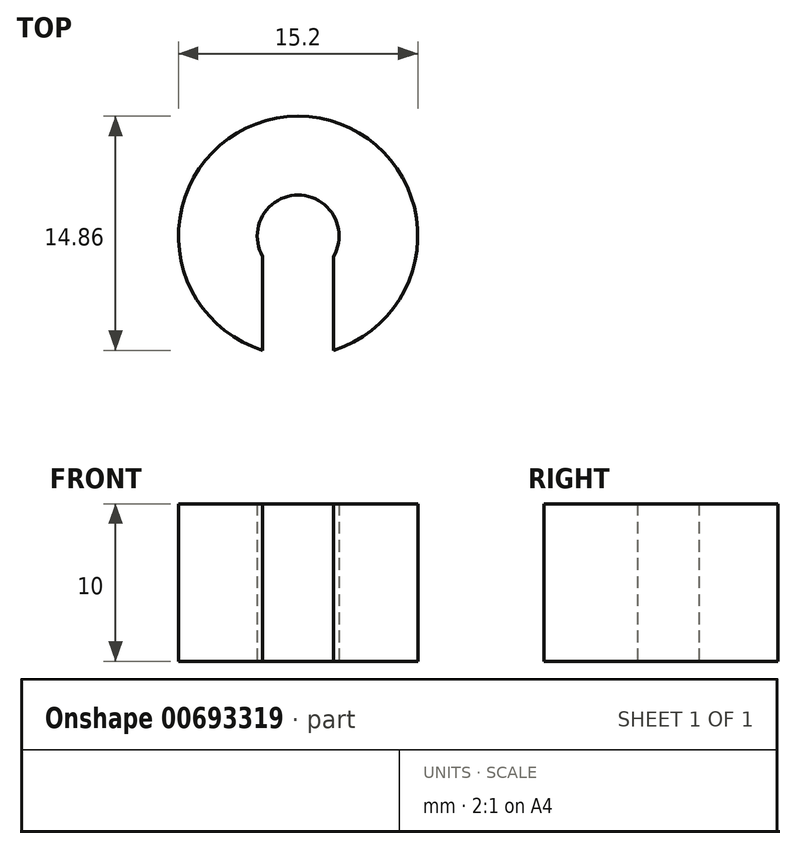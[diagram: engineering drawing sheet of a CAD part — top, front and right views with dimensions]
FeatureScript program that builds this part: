
annotation { "Feature Type Name" : "Feature", "Feature Type Description" : "" }
export const myFeature = defineFeature(function(context is Context, id is Id, definition is map)
    precondition{}
    {
        {
            var Q0;
            Q0=qCreatedBy(makeId("Top.planeOp"),FACE);
            var sketch = newSketch(context, id + "F0", { "sketchPlane" : qUnion([Q0])});
            skArc(sketch, "E0", {"start": v(2.25, -1.3) * mm, "mid": v(0, 2.6) * mm, "end": v(-2.25, -1.3) * mm});
            skArc(sketch, "E1", {"start": v(2.25, -7.26) * mm, "mid": v(0, 7.6) * mm, "end": v(-2.25, -7.26) * mm});
            skLineSegment(sketch, "E2", {"start": v(2.6, 0) * mm, "end": v(7.6, 0) * mm, "construction": true});
            skLineSegment(sketch, "E3", {"start": v(-2.25, -1.3) * mm, "end": v(-2.25, -7.26) * mm});
            skLineSegment(sketch, "E4.MirrorCS", {"start": v(2.25, -1.3) * mm, "end": v(2.25, -7.26) * mm});
            skSolve(sketch);
        }
        {
            var Q0;
            Q0=makeQuery(id+"F0.imprint","IMPRINT",FACE,{"disambiguationData":[TD([[makeQuery(id+"F0.imprint","IMPRINT",EDGE,{"derivedFrom":sQuery(id+"F0.wireOp",EDGE,"E0")}),-1.0]])]});
            extrude(context, id + "F1", {"entities" : qUnion([Q0]), "depth" : 10 * mm, "offsetDistance" : 25 * mm});
        }
    });
